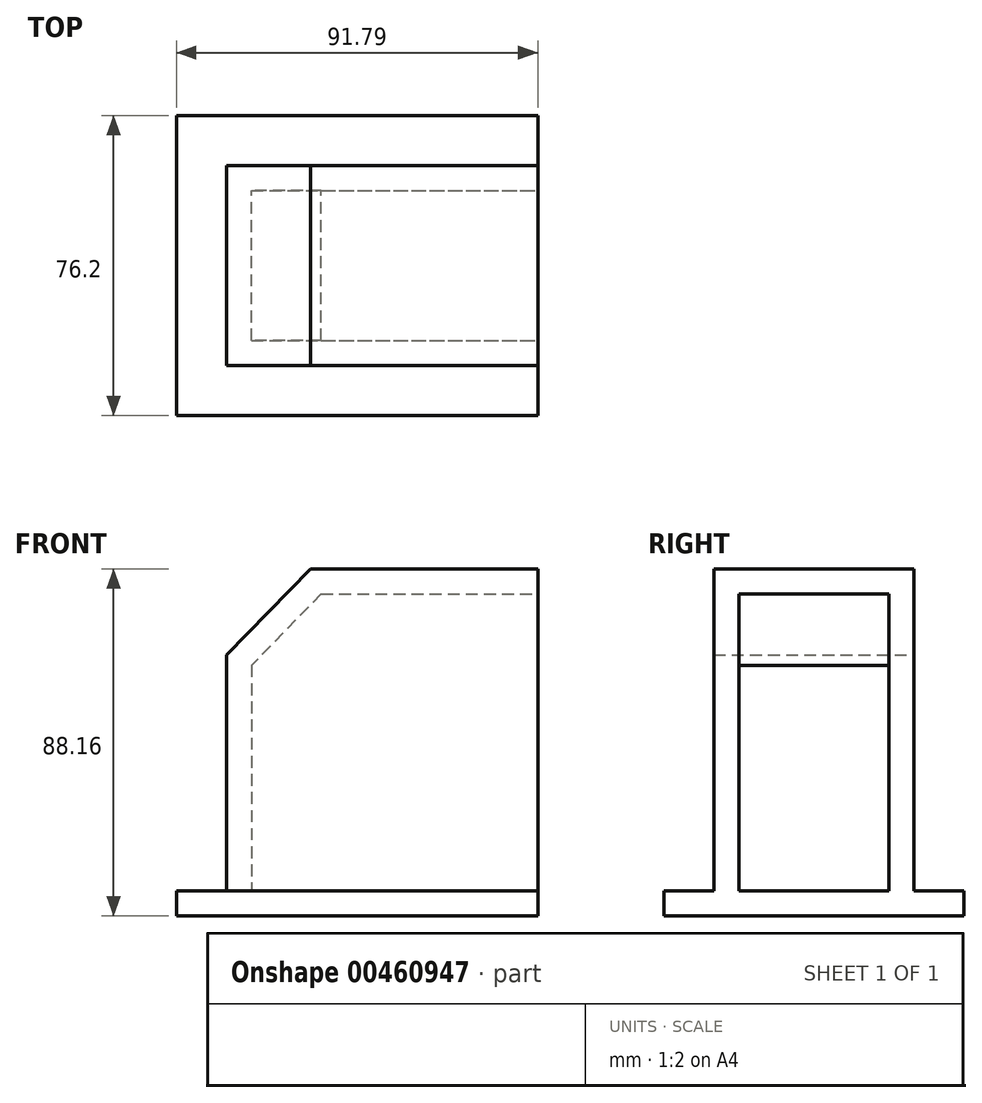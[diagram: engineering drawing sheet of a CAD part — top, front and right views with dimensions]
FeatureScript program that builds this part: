
annotation { "Feature Type Name" : "Feature", "Feature Type Description" : "" }
export const myFeature = defineFeature(function(context is Context, id is Id, definition is map)
    precondition{}
    {
        {
            var Q0;
            Q0=qCreatedBy(makeId("Front.planeOp"),FACE);
            var sketch = newSketch(context, id + "F0", { "sketchPlane" : qUnion([Q0])});
            skLineSegment(sketch, "E0.bottom", {"start": v(-19.36, 43.56) * mm, "end": v(38.38, 43.56) * mm});
            skLineSegment(sketch, "E0.top", {"start": v(-40.7, -38.25) * mm, "end": v(38.38, -38.25) * mm});
            skLineSegment(sketch, "E0.left", {"start": v(-40.7, 21.66) * mm, "end": v(-40.7, -38.25) * mm});
            skLineSegment(sketch, "E0.right", {"start": v(38.38, 43.56) * mm, "end": v(38.38, -38.25) * mm});
            skLineSegment(sketch, "E1", {"start": v(-19.23, 43.7) * mm, "end": v(-40.7, 21.66) * mm});
            skSolve(sketch);
        }
        {
            var Q0;
            Q0 = qSketchRegion(id + "F0", true);
            extrude(context, id + "F1", {"entities" : qUnion([Q0]), "depth" : 50.8 * mm});
        }
        {
            var Q0;
            Q0=makeQuery(id+"F1.opExtrude","SWEPT_FACE",FACE,{"disambiguationData":[OSD([sQuery(id+"F0.wireOp",EDGE,"E0.right")])]});
            var Q1;
            Q1=makeQuery(id+"F1.opExtrude","SWEPT_FACE",FACE,{"disambiguationData":[OSD([sQuery(id+"F0.wireOp",EDGE,"E0.top")])]});
            shell(context, id + "F2", {"entities" : qUnion([Q0, Q1]), "thickness" : 6.35 * mm});
        }
        {
            var Q0;
            Q0=makeQuery(id+"F1.opExtrude","SWEPT_FACE",FACE,{"disambiguationData":[OSD([sQuery(id+"F0.wireOp",EDGE,"E0.top")])]});
            var sketch = newSketch(context, id + "F3", { "sketchPlane" : qUnion([Q0])});
            skPoint(sketch, "E2", {"position": v(38.38, 63.5) * mm});
            skLineSegment(sketch, "E3.bottom", {"start": v(38.38, 63.5) * mm, "end": v(-53.4, 63.5) * mm});
            skLineSegment(sketch, "E3.top", {"start": v(38.38, -12.7) * mm, "end": v(-53.4, -12.7) * mm});
            skLineSegment(sketch, "E3.left", {"start": v(38.38, 63.5) * mm, "end": v(38.38, -12.7) * mm});
            skLineSegment(sketch, "E3.right", {"start": v(-53.4, 63.5) * mm, "end": v(-53.4, -12.7) * mm});
            skSolve(sketch);
        }
        {
            var Q0;
            Q0 = qSketchRegion(id + "F3", true);
            extrude(context, id + "F4", {"entities" : qUnion([Q0]), "operationType" : NewBodyOperationType.ADD, "depth" : 6.35 * mm});
        }
    });
